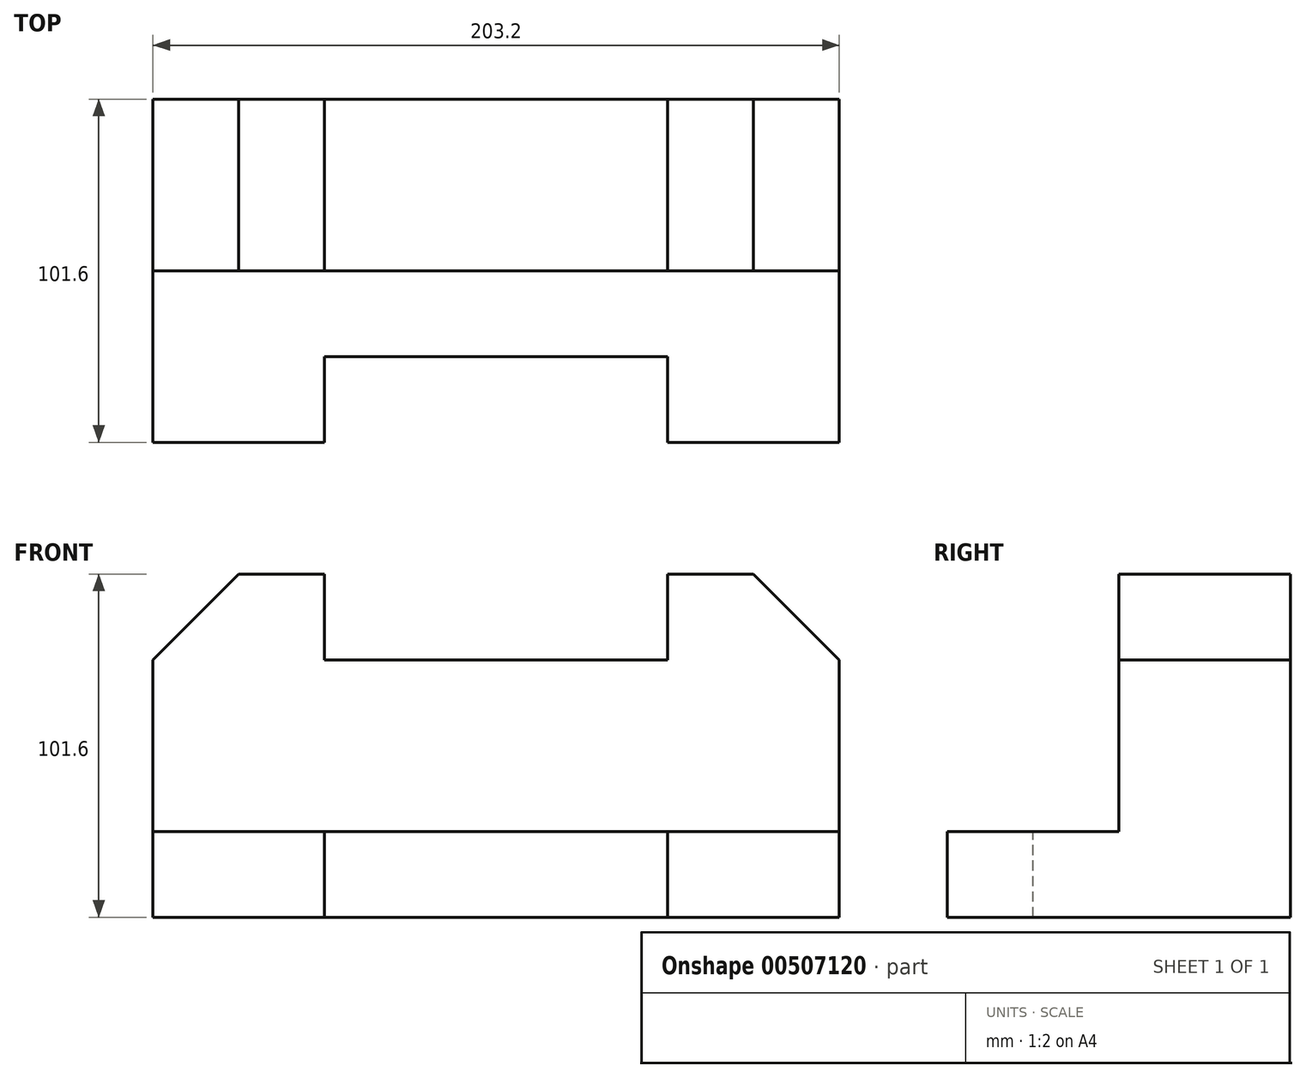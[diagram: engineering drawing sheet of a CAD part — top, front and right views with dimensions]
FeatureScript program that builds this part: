
annotation { "Feature Type Name" : "Feature", "Feature Type Description" : "" }
export const myFeature = defineFeature(function(context is Context, id is Id, definition is map)
    precondition{}
    {
        {
            var Q0;
            Q0=qCreatedBy(makeId("Top.planeOp"),FACE);
            var sketch = newSketch(context, id + "F0", { "sketchPlane" : qUnion([Q0])});
            skLineSegment(sketch, "E0.bottom", {"start": v(103.52, 50.8) * mm, "end": v(-99.68, 50.8) * mm});
            skLineSegment(sketch, "E0.top", {"start": v(103.52, -50.8) * mm, "end": v(-99.68, -50.8) * mm});
            skLineSegment(sketch, "E0.left", {"start": v(103.52, 50.8) * mm, "end": v(103.52, -50.8) * mm});
            skLineSegment(sketch, "E0.right", {"start": v(-99.68, 50.8) * mm, "end": v(-99.68, -50.8) * mm});
            skPoint(sketch, "E0.middle", {"position": v(1.92, 0) * mm});
            skSolve(sketch);
        }
        {
            var Q0;
            Q0 = qSketchRegion(id + "F0", true);
            extrude(context, id + "F1", {"entities" : qUnion([Q0]), "depth" : 101.6 * mm});
        }
        {
            var Q0;
            Q0=makeQuery(id+"F1.opExtrude","CAP_FACE",FACE,{"disambiguationData":[OSD([sQuery(id+"F0.wireOp",EDGE,"E0.bottom"),sQuery(id+"F0.wireOp",EDGE,"E0.top"),sQuery(id+"F0.wireOp",EDGE,"E0.left"),sQuery(id+"F0.wireOp",EDGE,"E0.right")])],"isStart":false});
            var sketch = newSketch(context, id + "F2", { "sketchPlane" : qUnion([Q0])});
            skLineSegment(sketch, "E1.bottom", {"start": v(-99.68, -50.8) * mm, "end": v(103.52, -50.8) * mm});
            skLineSegment(sketch, "E1.top", {"start": v(-99.68, 0) * mm, "end": v(103.52, 0) * mm});
            skLineSegment(sketch, "E1.left", {"start": v(-99.68, -50.8) * mm, "end": v(-99.68, 0) * mm});
            skLineSegment(sketch, "E1.right", {"start": v(103.52, -50.8) * mm, "end": v(103.52, 0) * mm});
            skSolve(sketch);
        }
        {
            var Q0;
            Q0 = qSketchRegion(id + "F2", true);
            extrude(context, id + "F3", {"entities" : qUnion([Q0]), "operationType" : NewBodyOperationType.REMOVE, "oppositeDirection" : true, "depth" : 76.2 * mm});
        }
        {
            var Q0;
            Q0=makeQuery(id+"F3.boolean.opBoolean","COPY",FACE,{"derivedFrom":makeQuery(id+"F3.opExtrude","CAP_FACE",FACE,{"disambiguationData":[OSD([sQuery(id+"F2.wireOp",EDGE,"E1.bottom"),sQuery(id+"F2.wireOp",EDGE,"E1.top"),sQuery(id+"F2.wireOp",EDGE,"E1.left"),sQuery(id+"F2.wireOp",EDGE,"E1.right")])],"isStart":false})});
            var sketch = newSketch(context, id + "F4", { "sketchPlane" : qUnion([Q0])});
            skLineSegment(sketch, "E2.bottom", {"start": v(-48.88, -50.8) * mm, "end": v(52.72, -50.8) * mm});
            skLineSegment(sketch, "E2.top", {"start": v(-48.88, -25.4) * mm, "end": v(52.72, -25.4) * mm});
            skLineSegment(sketch, "E2.left", {"start": v(-48.88, -50.8) * mm, "end": v(-48.88, -25.4) * mm});
            skLineSegment(sketch, "E2.right", {"start": v(52.72, -50.8) * mm, "end": v(52.72, -25.4) * mm});
            skSolve(sketch);
        }
        {
            var Q0;
            Q0 = qSketchRegion(id + "F4", true);
            extrude(context, id + "F5", {"entities" : qUnion([Q0]), "operationType" : NewBodyOperationType.REMOVE, "oppositeDirection" : true, "depth" : 25.4 * mm});
        }
        {
            var Q0;
            Q0=makeQuery(id+"F1.opExtrude","CAP_FACE",FACE,{"disambiguationData":[OSD([sQuery(id+"F0.wireOp",EDGE,"E0.bottom"),sQuery(id+"F0.wireOp",EDGE,"E0.top"),sQuery(id+"F0.wireOp",EDGE,"E0.left"),sQuery(id+"F0.wireOp",EDGE,"E0.right")])],"isStart":false});
            var sketch = newSketch(context, id + "F6", { "sketchPlane" : qUnion([Q0])});
            skLineSegment(sketch, "E3.bottom", {"start": v(-48.88, 50.8) * mm, "end": v(52.72, 50.8) * mm});
            skLineSegment(sketch, "E3.top", {"start": v(-48.88, 0) * mm, "end": v(52.72, 0) * mm});
            skLineSegment(sketch, "E3.left", {"start": v(-48.88, 50.8) * mm, "end": v(-48.88, 0) * mm});
            skLineSegment(sketch, "E3.right", {"start": v(52.72, 50.8) * mm, "end": v(52.72, 0) * mm});
            skSolve(sketch);
        }
        {
            var Q0;
            Q0 = qSketchRegion(id + "F6", true);
            extrude(context, id + "F7", {"entities" : qUnion([Q0]), "operationType" : NewBodyOperationType.REMOVE, "oppositeDirection" : true, "depth" : 25.4 * mm});
        }
        {
            var Q0;
            Q0=makeQuery(id+"F3.boolean.opBoolean","COPY",FACE,{"derivedFrom":makeQuery(id+"F3.opExtrude","SWEPT_FACE",FACE,{"disambiguationData":[OSD([sQuery(id+"F2.wireOp",EDGE,"E1.top")])]})});
            var sketch = newSketch(context, id + "F8", { "sketchPlane" : qUnion([Q0])});
            skLineSegment(sketch, "E4.bottom", {"start": v(103.52, 101.6) * mm, "end": v(78.12, 101.6) * mm});
            skLineSegment(sketch, "E4.top", {"start": v(103.52, 76.2) * mm, "end": v(78.12, 76.2) * mm});
            skLineSegment(sketch, "E4.left", {"start": v(103.52, 101.6) * mm, "end": v(103.52, 76.2) * mm});
            skLineSegment(sketch, "E4.right", {"start": v(78.12, 101.6) * mm, "end": v(78.12, 76.2) * mm});
            skLineSegment(sketch, "E5", {"start": v(78.12, 101.6) * mm, "end": v(103.52, 76.2) * mm});
            skSolve(sketch);
        }
        {
            var Q0;
            Q0=makeQuery(id+"F8.imprint","IMPRINT",FACE,{"disambiguationData":[TD([[makeQuery(id+"F8.imprint","IMPRINT",EDGE,{"derivedFrom":sQuery(id+"F8.wireOp",EDGE,"E4.bottom")}),-1.0]])]});
            extrude(context, id + "F9", {"entities" : qUnion([Q0]), "operationType" : NewBodyOperationType.REMOVE, "oppositeDirection" : true, "depth" : 50.8 * mm});
        }
        {
            var Q0;
            Q0=makeQuery(id+"F3.boolean.opBoolean","COPY",FACE,{"derivedFrom":makeQuery(id+"F3.opExtrude","SWEPT_FACE",FACE,{"disambiguationData":[OSD([sQuery(id+"F2.wireOp",EDGE,"E1.top")])]})});
            var sketch = newSketch(context, id + "F10", { "sketchPlane" : qUnion([Q0])});
            skLineSegment(sketch, "E6.bottom", {"start": v(-99.68, 101.6) * mm, "end": v(-74.28, 101.6) * mm});
            skLineSegment(sketch, "E6.top", {"start": v(-99.68, 76.2) * mm, "end": v(-74.28, 76.2) * mm});
            skLineSegment(sketch, "E6.left", {"start": v(-99.68, 101.6) * mm, "end": v(-99.68, 76.2) * mm});
            skLineSegment(sketch, "E6.right", {"start": v(-74.28, 101.6) * mm, "end": v(-74.28, 76.2) * mm});
            skLineSegment(sketch, "E7", {"start": v(-74.28, 101.6) * mm, "end": v(-99.68, 76.2) * mm});
            skSolve(sketch);
        }
        {
            var Q0;
            Q0=makeQuery(id+"F10.imprint","IMPRINT",FACE,{"disambiguationData":[TD([[makeQuery(id+"F10.imprint","IMPRINT",EDGE,{"derivedFrom":sQuery(id+"F10.wireOp",EDGE,"E6.bottom")}),-1.0]])]});
            extrude(context, id + "F11", {"entities" : qUnion([Q0]), "operationType" : NewBodyOperationType.REMOVE, "oppositeDirection" : true, "depth" : 50.8 * mm});
        }
    });
